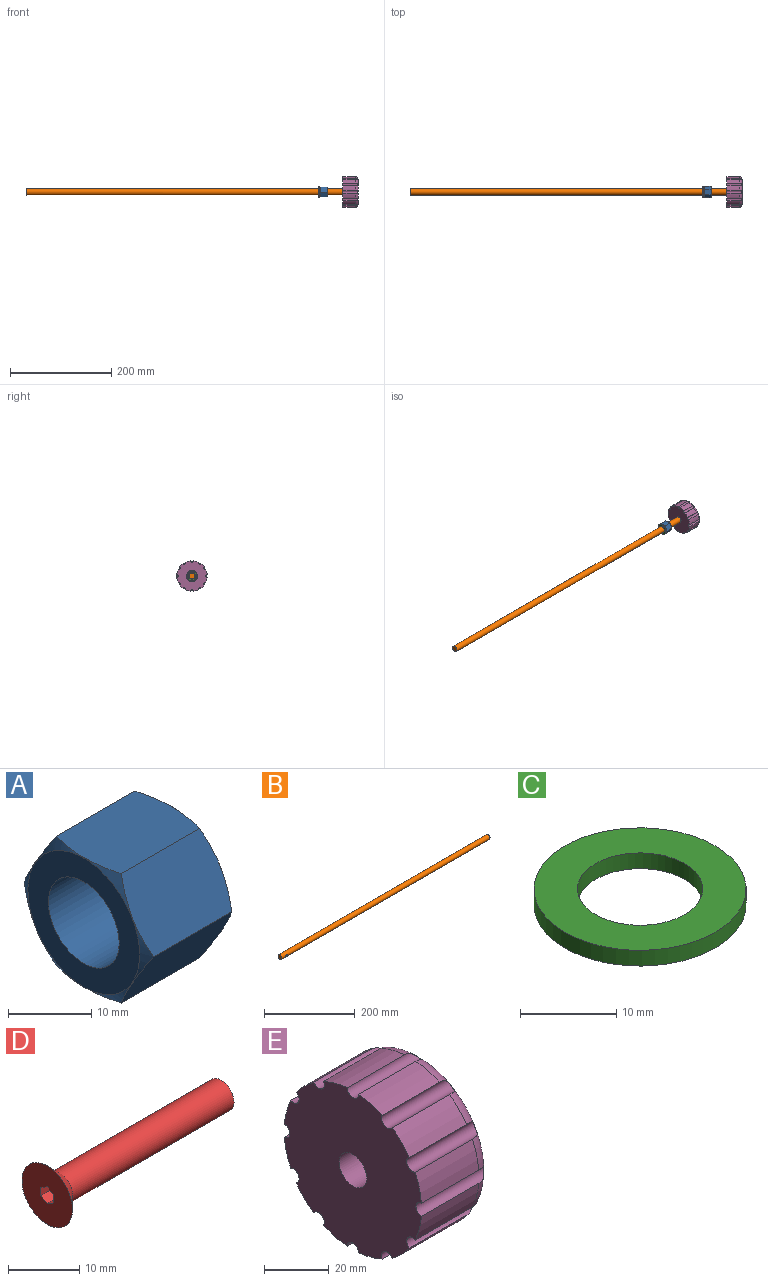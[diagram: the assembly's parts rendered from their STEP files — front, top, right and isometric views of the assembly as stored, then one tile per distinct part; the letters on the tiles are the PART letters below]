
ASSEMBLY  parts=5 mates=4
PART A: 11 faces, bbox 15x21.9x21.9 mm
  f0: plane 18.94x18.94mm, normal (1,0,0), area 168.6mm2, adj f1,f4
  f1: cylinder r=6mm len=15mm, axis (-1,0,0), area 565.5mm2, adj f0,f2
  f2: plane 18.94x18.94mm, normal (-1,0,0), area 168.6mm2, adj f1,f3
  f3: cone r=9.47mm half-angle=60deg, axis (1,0,0), area 35.7mm2, adj f2,f5,f6,f7,f8,f9,f10
  f4: cone r=9.47mm half-angle=60deg, axis (-1,0,0), area 35.7mm2, adj f0,f5,f6,f7,f8,f9,f10
  f5: plane 14.97x9.5mm, normal (0,-0.87,-0.5), area 157.8mm2, adj f3,f4,f6,f10
  f6: plane 14.97x9.5mm, normal (0,-0.87,0.5), area 157.8mm2, adj f3,f4,f5,f7
  f7: plane 14.97x10.98mm, normal (0,0,1), area 157.8mm2, adj f3,f4,f6,f8
  f8: plane 14.97x9.5mm, normal (0,0.87,0.5), area 157.8mm2, adj f3,f4,f7,f9
  f9: plane 14.97x9.5mm, normal (0,0.87,-0.5), area 157.8mm2, adj f3,f4,f8,f10
  f10: plane 14.97x10.98mm, normal (0,0,-1), area 157.8mm2, adj f3,f4,f5,f9
PART B: 4 faces, bbox 650x12x12 mm
  f0: cylinder r=6mm len=650mm, axis (-1,0,0), area 24464.2mm2, adj f1,f2,f3
  f1: plane 12x12mm, normal (1,0,0), area 113.1mm2, adj f0
  f2: plane 12x12mm, normal (-1,0,0), area 113.1mm2, adj f0
  f3: cylinder r=2.5mm len=12mm, axis (0,-1,0), area 180mm2, adj f0
PART C: 4 faces, bbox 22x22x2 mm
  f0: cylinder r=6.5mm len=13mm, axis (0,0,-1), area 81.7mm2, adj f2,f3
  f1: cylinder r=11mm len=22mm, axis (0,0,-1), area 138.2mm2, adj f2,f3
  f2: plane 22x22mm, normal (0,0,1), area 247.4mm2, adj f0,f1
  f3: plane 22x22mm, normal (0,0,-1), area 247.4mm2, adj f0,f1
PART D: 11 faces, bbox 34.5x10x10 mm
  f0: plane 10x10mm, normal (-1,0,0), area 73.1mm2, adj f3,f4,f5,f6,f7,f8,f9
  f1: plane 5x5mm, normal (1,0,0), area 19.6mm2, adj f2
  f2: cylinder r=2.5mm len=32mm, axis (-1,0,0), area 502.7mm2, adj f1,f3
  f3: cone r=5mm half-angle=45deg, axis (-1,0,0), area 83.3mm2, adj f0,f2
  f4: plane 2x1.25mm, normal (0,0.5,0.87), area 2.9mm2, adj f0,f5,f9,f10
  f5: plane 2x1.44mm, normal (0,1,0), area 2.9mm2, adj f0,f4,f6,f10
  f6: plane 2x1.25mm, normal (0,0.5,-0.87), area 2.9mm2, adj f0,f5,f7,f10
  f7: plane 2x1.25mm, normal (0,-0.5,-0.87), area 2.9mm2, adj f0,f6,f8,f10
  f8: plane 2x1.44mm, normal (0,-1,0), area 2.9mm2, adj f0,f7,f9,f10
  f9: plane 2x1.25mm, normal (0,-0.5,0.87), area 2.9mm2, adj f0,f4,f8,f10
  f10: plane 2.89x2.5mm, normal (-1,0,0), area 5.4mm2, adj f4,f5,f6,f7,f8,f9
PART E: 34 faces, bbox 30x64.9x64.9 mm
  f0: cylinder r=2.5mm len=6.9mm, axis (-1,0,0), area 49.2mm2, adj f1,f2,f14,f31,f32,f33
  f1: cylinder r=30mm len=25mm, axis (-1,0,0), area 252.2mm2, adj f0,f3,f14,f17,f25,f31
  f2: cylinder r=30mm len=25mm, axis (-1,0,0), area 252.2mm2, adj f0,f3,f14,f17,f24,f32
  f3: cylinder r=2.5mm len=16.23mm, axis (-1,0,0), area 113.7mm2, adj f1,f2,f17,f31,f32,f33
  f4: cylinder r=2.75mm len=21.81mm, axis (0,-1,0), area 371mm2, adj f18,f33
  f5: cylinder r=30mm len=25mm, axis (-1,0,0), area 267.7mm2, adj f14,f17,f26,f30
  f6: cylinder r=30mm len=25mm, axis (-1,0,0), area 267.7mm2, adj f14,f17,f29,f30
  f7: cylinder r=30mm len=25mm, axis (-1,0,0), area 267.7mm2, adj f14,f17,f28,f29
  f8: cylinder r=30mm len=25mm, axis (-1,0,0), area 267.7mm2, adj f14,f17,f27,f28
  f9: cylinder r=30mm len=25mm, axis (-1,0,0), area 267.7mm2, adj f14,f17,f25,f26
  f10: cylinder r=30mm len=25mm, axis (-1,0,0), area 267.7mm2, adj f14,f17,f23,f24
  f11: cylinder r=30mm len=25mm, axis (-1,0,0), area 267.7mm2, adj f14,f17,f22,f23
  f12: cylinder r=30mm len=25mm, axis (-1,0,0), area 267.7mm2, adj f14,f17,f21,f22
  f13: cylinder r=30mm len=25mm, axis (-1,0,0), area 267.7mm2, adj f14,f17,f20,f21
  f14: plane 59.79x59.79mm, normal (-1,0,0), area 2598.6mm2, adj f0,f1,f2,f5,f6,f7,f8,f9
  f15: cylinder r=30mm len=25mm, axis (-1,0,0), area 267.7mm2, adj f14,f17,f20,f27
  f16: plane 50x50mm, normal (1,0,0), area 1963.5mm2, adj f17
  f17: torus R=25mm, axis (1,0,0), area 1122mm2, adj f1,f2,f3,f5,f6,f7,f8,f9
  f18: cylinder r=6mm len=25mm, axis (-1,0,0), area 918mm2, adj f4,f14,f19
  f19: plane 12x12mm, normal (-1,0,0), area 113.1mm2, adj f18
  f20: cylinder r=2.5mm len=29.33mm, axis (-1,0,0), area 217.4mm2, adj f13,f14,f15,f17
  f21: cylinder r=2.5mm len=29.33mm, axis (-1,0,0), area 217.4mm2, adj f12,f13,f14,f17
  f22: cylinder r=2.5mm len=29.33mm, axis (-1,0,0), area 217.4mm2, adj f11,f12,f14,f17
  f23: cylinder r=2.5mm len=29.33mm, axis (-1,0,0), area 217.4mm2, adj f10,f11,f14,f17
  f24: cylinder r=2.5mm len=29.33mm, axis (-1,0,0), area 217.4mm2, adj f2,f10,f14,f17
  f25: cylinder r=2.5mm len=29.33mm, axis (-1,0,0), area 217.4mm2, adj f1,f9,f14,f17
  f26: cylinder r=2.5mm len=29.33mm, axis (-1,0,0), area 217.4mm2, adj f5,f9,f14,f17
  f27: cylinder r=2.5mm len=29.33mm, axis (-1,0,0), area 217.4mm2, adj f8,f14,f15,f17
  f28: cylinder r=2.5mm len=29.33mm, axis (-1,0,0), area 217.4mm2, adj f7,f8,f14,f17
  f29: cylinder r=2.5mm len=29.33mm, axis (-1,0,0), area 217.4mm2, adj f6,f7,f14,f17
  f30: cylinder r=2.5mm len=29.33mm, axis (-1,0,0), area 217.4mm2, adj f5,f6,f14,f17
  f31: cylinder r=5mm len=8.74mm, axis (0,1,0), area 3.3mm2, adj f0,f1,f3,f33
  f32: cylinder r=5mm len=8.74mm, axis (0,1,0), area 3.3mm2, adj f0,f2,f3,f33
  f33: cone r=2.5mm half-angle=45deg, axis (0,1,0), area 57.4mm2, adj f0,f3,f4,f31,f32
PLACE A rot(axis=(0,1,0),180deg) t=(375.42,24.01,-76.93)mm
PLACE B rot(axis=(0,1,0),180deg) t=(430.42,24.01,-76.93)mm
PLACE C rot(axis=(-0.71,0,-0.71),180deg) t=(358.42,24.01,-76.93)mm
PLACE D rot(axis=(-0.58,0.58,-0.58),120deg) t=(415.42,53.65,-76.93)mm
PLACE E t=(405.42,24.01,-76.93)mm
MATE fastened E.f18 <-> B.f0  axis (-1,0,0) through (430.42,24.01,-76.93)mm
MATE revolute C.f0 <-> A.f3  axis (1,0,0) through (360.42,24.01,-76.93)mm
MATE fastened D.f2 <-> E.f4  axis (0,1,0) through (415.42,51.15,-76.93)mm
MATE fastened A.f3 <-> E.f1  axis (1,0,0) through (375.42,24.01,-76.93)mm
